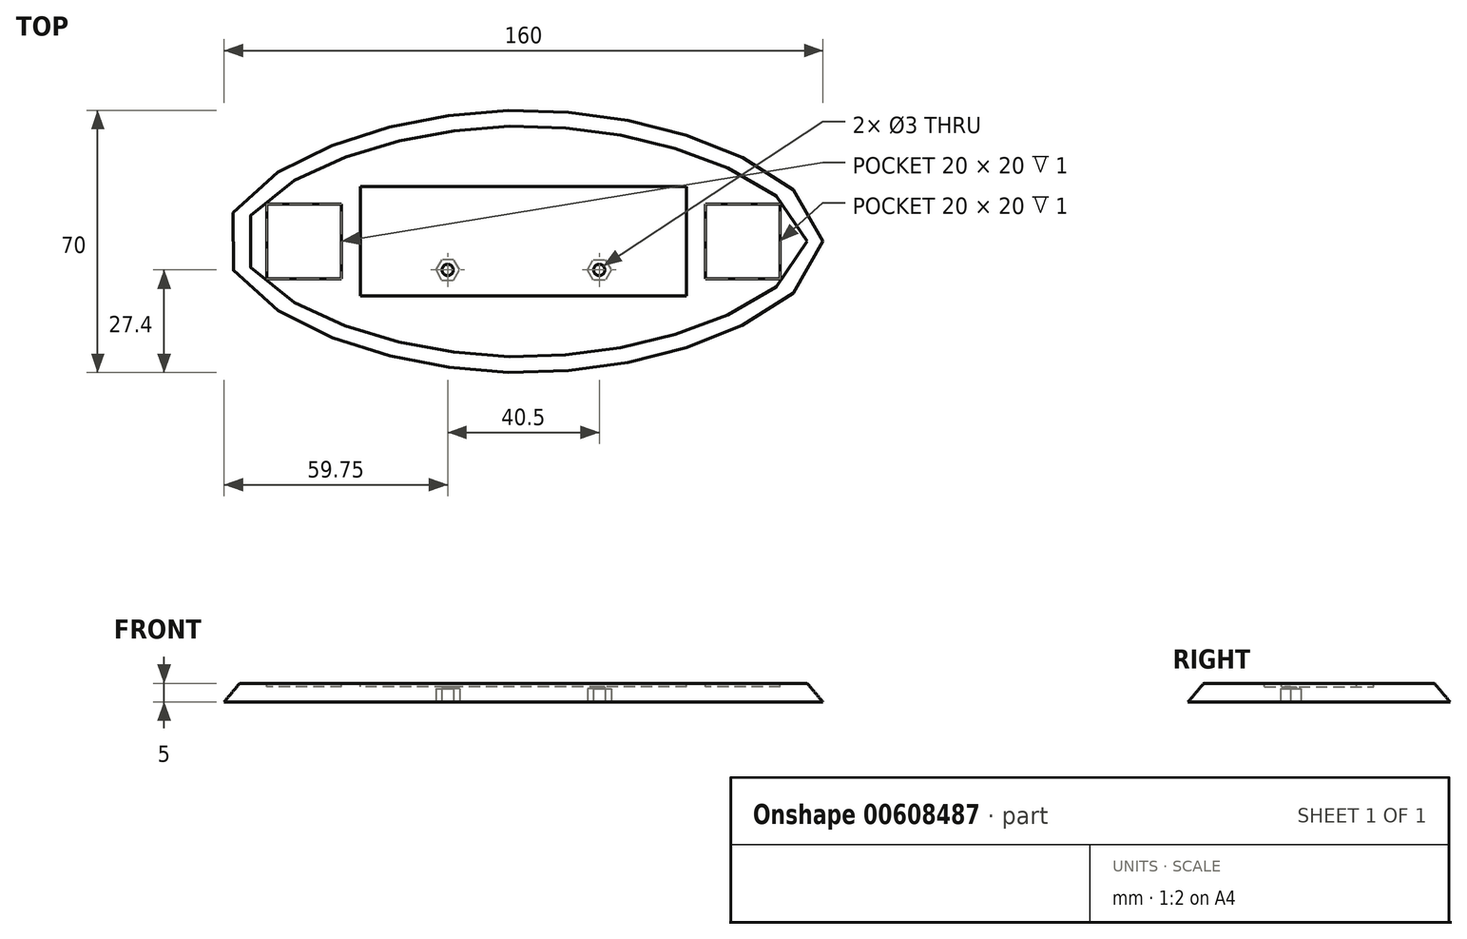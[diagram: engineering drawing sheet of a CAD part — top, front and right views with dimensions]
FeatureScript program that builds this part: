
annotation { "Feature Type Name" : "Feature", "Feature Type Description" : "" }
export const myFeature = defineFeature(function(context is Context, id is Id, definition is map)
    precondition{}
    {
        {
            var Q0;
            Q0=qCreatedBy(makeId("Top.planeOp"),FACE);
            var sketch = newSketch(context, id + "F0", { "sketchPlane" : qUnion([Q0])});
            skLineSegment(sketch, "E0", {"start": v(-80, 0) * mm, "end": v(80, 0) * mm, "construction": true});
            skPoint(sketch, "E1", {"position": v(0, 0) * mm});
            skFitSpline(sketch, "E2", {"points": [v(-80, 0) * mm, v(0, 35) * mm, v(80, 0) * mm, v(0, -35) * mm, v(-80, 0) * mm]});
            skLineSegment(sketch, "E3", {"start": v(0, 35) * mm, "end": v(0, -35) * mm, "construction": true});
            skSolve(sketch);
        }
        {
            var Q0;
            Q0 = qSketchRegion(id + "F0", true);
            extrude(context, id + "F1", {"entities" : qUnion([Q0]), "depth" : 5 * mm, "offsetDistance" : 25 * mm, "hasDraft" : true, "draftAngle" : 40 * degree, "draftPullDirection" : true});
        }
        {
            var Q0;
            Q0=makeQuery(id+"F1.opExtrude","CAP_FACE",FACE,{"disambiguationData":[OSD([sQuery(id+"F0.wireOp",EDGE,"E2")])],"isStart":false});
            var sketch = newSketch(context, id + "F2", { "sketchPlane" : qUnion([Q0])});
            skLineSegment(sketch, "E4.bottom", {"start": v(43.6, -14.6) * mm, "end": v(-43.6, -14.6) * mm});
            skLineSegment(sketch, "E4.top", {"start": v(43.6, 14.6) * mm, "end": v(-43.6, 14.6) * mm});
            skLineSegment(sketch, "E4.left", {"start": v(43.6, -14.6) * mm, "end": v(43.6, 14.6) * mm});
            skLineSegment(sketch, "E4.right", {"start": v(-43.6, -14.6) * mm, "end": v(-43.6, 14.6) * mm});
            skPoint(sketch, "E4.middle", {"position": v(0, 0) * mm});
            skLineSegment(sketch, "E5.bottom", {"start": v(-48.6, -10) * mm, "end": v(-68.6, -10) * mm});
            skLineSegment(sketch, "E5.top", {"start": v(-48.6, 10) * mm, "end": v(-68.6, 10) * mm});
            skLineSegment(sketch, "E5.left", {"start": v(-48.6, -10) * mm, "end": v(-48.6, 10) * mm});
            skLineSegment(sketch, "E5.right", {"start": v(-68.6, -10) * mm, "end": v(-68.6, 10) * mm});
            skPoint(sketch, "E5.middle", {"position": v(-58.6, 0) * mm});
            skLineSegment(sketch, "E6.bottom", {"start": v(68.6, -10) * mm, "end": v(48.6, -10) * mm});
            skLineSegment(sketch, "E6.top", {"start": v(68.6, 10) * mm, "end": v(48.6, 10) * mm});
            skLineSegment(sketch, "E6.left", {"start": v(68.6, -10) * mm, "end": v(68.6, 10) * mm});
            skLineSegment(sketch, "E6.right", {"start": v(48.6, -10) * mm, "end": v(48.6, 10) * mm});
            skPoint(sketch, "E6.middle", {"position": v(58.6, 0) * mm});
            skLineSegment(sketch, "E7", {"start": v(0, 0) * mm, "end": v(0, 14.6) * mm, "construction": true});
            skSolve(sketch);
        }
        {
            var Q0;
            Q0 = qSketchRegion(id + "F2", true);
            extrude(context, id + "F3", {"entities" : qUnion([Q0]), "operationType" : NewBodyOperationType.REMOVE, "oppositeDirection" : true, "depth" : 1 * mm, "offsetDistance" : 25 * mm});
        }
        {
            var Q0;
            Q0=makeQuery(id+"F1.opExtrude","CAP_FACE",FACE,{"disambiguationData":[OSD([sQuery(id+"F0.wireOp",EDGE,"E2")])],"isStart":true});
            var sketch = newSketch(context, id + "F4", { "sketchPlane" : qUnion([Q0])});
            skCircle(sketch, "E8.cCircle", {"center": v(-20.25, 7.6) * mm, "radius": 2.75 * mm, "construction": true});
            skLineSegment(sketch, "E8.0", {"start": v(-18.66, 4.85) * mm, "end": v(-21.84, 4.85) * mm});
            skLineSegment(sketch, "E8.1", {"start": v(-21.84, 4.85) * mm, "end": v(-23.43, 7.6) * mm});
            skLineSegment(sketch, "E8.2", {"start": v(-23.43, 7.6) * mm, "end": v(-21.84, 10.35) * mm});
            skLineSegment(sketch, "E8.3", {"start": v(-21.84, 10.35) * mm, "end": v(-18.66, 10.35) * mm});
            skLineSegment(sketch, "E8.4", {"start": v(-18.66, 10.35) * mm, "end": v(-17.07, 7.6) * mm});
            skLineSegment(sketch, "E8.5", {"start": v(-17.07, 7.6) * mm, "end": v(-18.66, 4.85) * mm});
            skPoint(sketch, "E8.0.midPoint", {"position": v(-20.25, 4.85) * mm});
            skLineSegment(sketch, "E9.bottom", {"start": v(43.6, -14.6) * mm, "end": v(-43.6, -14.6) * mm, "construction": true});
            skLineSegment(sketch, "E9.top", {"start": v(43.6, 14.6) * mm, "end": v(-43.6, 14.6) * mm, "construction": true});
            skLineSegment(sketch, "E9.left", {"start": v(43.6, -14.6) * mm, "end": v(43.6, 14.6) * mm, "construction": true});
            skLineSegment(sketch, "E9.right", {"start": v(-43.6, -14.6) * mm, "end": v(-43.6, 14.6) * mm, "construction": true});
            skPoint(sketch, "E9.middle", {"position": v(0, 0) * mm});
            skLineSegment(sketch, "E10.MirrorCS", {"start": v(18.66, 10.35) * mm, "end": v(17.07, 7.6) * mm});
            skLineSegment(sketch, "E11.MirrorCS", {"start": v(21.84, 10.35) * mm, "end": v(18.66, 10.35) * mm});
            skLineSegment(sketch, "E12.MirrorCS", {"start": v(23.43, 7.6) * mm, "end": v(21.84, 10.35) * mm});
            skLineSegment(sketch, "E13.MirrorCS", {"start": v(21.84, 4.85) * mm, "end": v(23.43, 7.6) * mm});
            skLineSegment(sketch, "E14.MirrorCS", {"start": v(18.66, 4.85) * mm, "end": v(21.84, 4.85) * mm});
            skLineSegment(sketch, "E15.MirrorCS", {"start": v(17.07, 7.6) * mm, "end": v(18.66, 4.85) * mm});
            skCircle(sketch, "E16", {"center": v(-20.25, 7.6) * mm, "radius": 1.5 * mm});
            skCircle(sketch, "E17.MirrorC", {"center": v(20.25, 7.6) * mm, "radius": 1.5 * mm});
            skSolve(sketch);
        }
        {
            var Q0;
            Q0 = qSketchRegion(id + "F4", true);
            extrude(context, id + "F5", {"entities" : qUnion([Q0]), "operationType" : NewBodyOperationType.REMOVE, "oppositeDirection" : true, "depth" : 3.5 * mm, "offsetDistance" : 25 * mm});
        }
        {
            var Q0;
            Q0=makeQuery(id+"F5.boolean.opBoolean","SPLIT",FACE,{"disambiguationData":[TD([makeQuery(id+"F5.opExtrude","SWEPT_FACE",FACE,{"disambiguationData":[OSD([sQuery(id+"F4.wireOp",EDGE,"E16")])]})])],"derivedFrom":makeQuery(id+"F1.opExtrude","CAP_FACE",FACE,{"disambiguationData":[OSD([sQuery(id+"F0.wireOp",EDGE,"E2")])],"isStart":true})});
            var Q1;
            Q1=makeQuery(id+"F5.boolean.opBoolean","SPLIT",FACE,{"disambiguationData":[TD([makeQuery(id+"F5.opExtrude","SWEPT_FACE",FACE,{"disambiguationData":[OSD([sQuery(id+"F4.wireOp",EDGE,"E17.MirrorC")])]})])],"derivedFrom":makeQuery(id+"F1.opExtrude","CAP_FACE",FACE,{"disambiguationData":[OSD([sQuery(id+"F0.wireOp",EDGE,"E2")])],"isStart":true})});
            extrude(context, id + "F6", {"entities" : qUnion([Q0, Q1]), "operationType" : NewBodyOperationType.REMOVE, "endBound" : BoundingType.UP_TO_NEXT, "oppositeDirection" : true, "depth" : 25 * mm, "offsetDistance" : 25 * mm});
        }
    });
